# Revit family: Domotics-DomesticRanges-GEWISS-CHORUS_COMMAND-PUSH-BUTTON_05M
name_source: partatom
category: Apparecchi elettrici
revit_build: Autodesk Revit 2016 (Build: 20161004_0715(x64)
units: mm (PartAtom-declared; Revit-internal decimal feet)

## family parameters
Condiviso = Sì
Host = Superficie
Mantenere orientamento annotazione = Sì
Numero OmniClass = 23.80.50.11.14
Punto di calcolo locali = Sì
Quota connettore circolare = Usa diametro
Taglio con vuoti quando caricato = Sì
Tipo di parte = Normale
Titolo OmniClass = Switches

## types (6) — shared parameters
Bidimensionale = bidimensionale pulsanti 05 : GW10162
Breaking capacity: = 1.25 In (200 position changes)
Catalogue = DOMOTICS
Catalogue Range = CHORUS - DOMESTIC RANGE
Category = Push-button
Electrocod = 0130
Glow Wire Test = 850°C
IDF = 75a35bb3-8328-4b3e-a169-8ecd7cf75c9a
IDT = 7b9cd6d0-4acf-4a4b-bc88-5334f44e4e2c
Immagine tipo = GW14162.jpg
Insulation resistance = > 5 MOhm
Larghezza pulsante = 12 mm  [stored 0.0393701 ft]
No. Chorus modules = 1/2
Number of poles = 1P
Produttore = GEWISS S.p.A.
Prolonged operation (no.of position changes) = 40.000 at In 250 V ac cosÃ˜=0,6
Prospetto di default = 1219 mm
Resistance at test voltage = 2000 V at 50 Hz for 1 minute
SEO = Push button
Simbolo_ = SIMBOLO PULSANTI : LUM
Standard; = EN 60669-1
Technical sheet = https://www.gewiss.com
Terminal grip on cable traction = > 50 N
Terminal tightening capacity flexible cables (mm2) = min. 0,75 - max. 2x4
Terminal tightening capacity rigid cables (mm2) = min. 0,5 - max. 2x2,5
Thermo-pressure with ball = 125
Tipo_ = CHORUS PULSANTI 05M_BASE : GW14162 - Titanio - Illuminabile localizzazione
URL = https://www.gewiss.com
Version file RFA = 19.0
Voltage = 250 V ac
Voltage: = 250 V ac
Wiring terminals = With screw

## per-type parameters (varying)
| type | Button key | Colour | Description: | Descrizione | EAN code | Modello | Type |
| GW10161 - White | Neutral | White | 1P NO - 10A | PUSH-BUTTON, 1/2M 1P NO 10A WHITE | 8011564261020 | GW10161 | General |
| GW14161 - Titanium | Neutral | Titanium | 1P NO - 10A | PUSH-BUTTON 1/2M 1P NO 10A TITANIUM | 8011564266018 | GW14161 | General |
| GW10162 - White - Illuminable | With diffuser | White | 1P NO - 10A illuminable | PUSH-BUTTON 1/2M 1P NO 10A ILL LOC WHITE | 8011564261037 | GW10162 | Backlit |
| GW12161 - Black | Neutral | Black | 1P NO - 10A | PUSH-BUTTON 1/2M 1P NO 10A BLACK | 8011564269415 | GW12161 | General |
| GW12162 - Black - Illuminable | With diffuser | Black | 1P NO - 10A illuminable | PUSH-BUTTON 1/2M 1P NO 10A ILL LOC BLACK | 8011564269422 | GW12162 | Backlit |
| GW14162 - Titanium - Illuminable | With diffuser | Titanium | 1P NO - 10A illuminable | P-BUTTON 1/2M 1P NO 10A ILL LOC TITANIUM | 8011564266025 | GW14162 | Backlit |

note: source unit labels omitted for Thermo-pressure with ball — the stored unit's dimension contradicts the parameter name (converter mislabeling)

note: [stored X ft] marks values corroborated as IEEE doubles in the binary element streams (Revit-internal decimal feet)

## geometry (parser evidence)
native form markers: Sweep x1
no freeform markers — native parametric forms only
